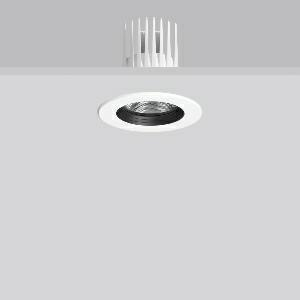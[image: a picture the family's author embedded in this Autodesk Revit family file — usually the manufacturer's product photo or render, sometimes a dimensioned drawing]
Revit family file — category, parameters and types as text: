
# Revit family: heledon_mini_e_901741_002_2_76_0b32
name_source: partatom
category: Lighting Fixtures
units: mm (PartAtom-declared; Revit-internal decimal feet)

## family parameters
Cut with Voids When Loaded = No
Host = Face
Light Source = No
Part Type = Normal
Room Calculation Point = No
Round Connector Dimension = Use Diameter
Shared = No

## types (1)
- HELEDON mini E (1 x LED Modul 927, 2300 lm, 2700)
    Apparent Load = 20 VA
    Approval mark = CE
    CIE Flux Codes = 99 100 100 100 100
    Color Rendering = 92
    Color Temperature = 2700
    Default Elevation = 1800 mm
    Description = Series: HELEDON mini
Round recessed downlight. Housing: die-cast aluminium, powder-coated. Black plastic ring and recessed LED to prevent glare from the side. Optical assembly with reflector made of MIRO-Silver with 98% total light reflection for outstanding efficiency - can be changed without tools. Best colour rendering index Ra>90. Suitable for Recessed ceiling mounting. Installation without tools thanks to spring fastening system. Including separate LED converter with connecting cable 600 mm.High quality converter without flickering and stroboscopic effect. Through-wiring box (5 pole) available as accessory. The following accessories can be mounted without use of tools: interchangeable lenses, decorative glasses, honeycomb louvre, clear and frosted diffusers, white interchangeable plastic ring. 
Colour: traffic white, matt (RAL 9016)
Diameter: 124 mm
Height: 3 mm
Cut-out diameter: 114 mm
Recess height: 170 mm
Luminaire: recess height: 120 mm
Lamp: LED
Socket: without socket
Colour temperature: 2700K
Colour rendering index (CRI): 92
System power: 20 W
Rated luminous flux: 2300 lm
Luminous efficiency: 115 lm/W
Control gear: Converter, dimmable, DALI
Protection class: II
Type of protection: IP 20
    Height = 0 mm  [stored 0 ft]
    Lamp = 1 x LED Modul 927
    Lamp Light Flux = 2300 lm
    Lamp count = 1
    Length = 124 mm  [stored 0.406824 ft]
    Lifetime = 50000 h
    Luminous efficacy = 115 lm/W
    Manufacturer = RZB
    ModVariant = No
    Model = 901741.002.2.76
    Mounting Place = Ceiling
    Mounting Type = Recessed
    Number of Poles = 1
    OnlyDefault = Yes
    Power Factor = 1
    Product Name = HELEDON mini E
    Product group = Recessed downlights
    ProductGroupID = 402
    Protection Class = Protection class II
    Protection Degree = IP 20
    RLX_Detail_Level = 1
    RLX_Emergency_Light_Flux = 0 lm
    RLX_Emergency_Type = 0
    RLX_Emergency_Type_DB = No
    RlxData = <blob elided: 124229 chars, md5=7a42af53>
    Socket = socket
    Standby Power = 0 W
    System Light Flux = 2300 lm
    System Power = 20 W
    Type Comments = Product without accessories
    Type Image = 901657.002.jpg
    URL = http://relux.com
    VarID = ---
    Voltage = 230 V
    Voltage Range = 220-240 V
    Weight = 0.00 kg
    Width = 0 mm  [stored 0 ft]

note: [stored X ft] marks values corroborated as IEEE doubles in the binary element streams (Revit-internal decimal feet)

## geometry (parser evidence)
native form markers: Blend x4, Sweep x11
no freeform markers — native parametric forms only
